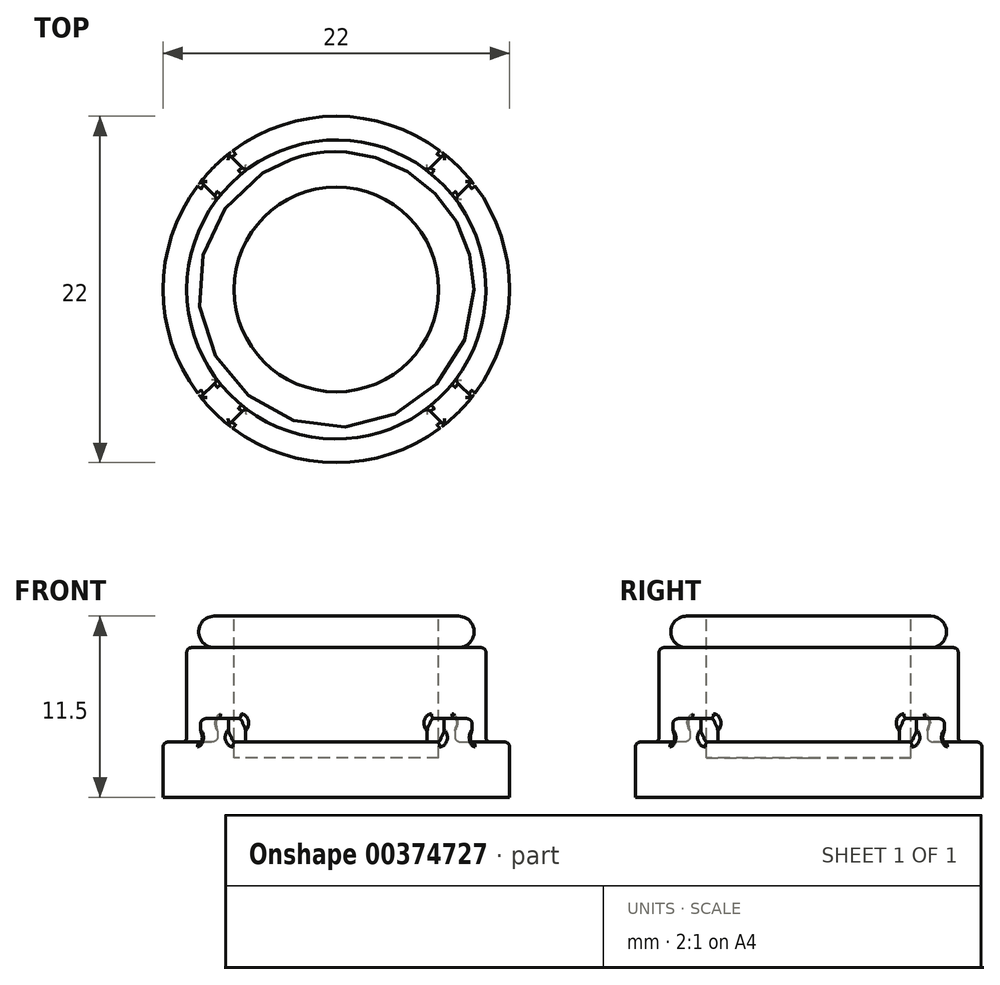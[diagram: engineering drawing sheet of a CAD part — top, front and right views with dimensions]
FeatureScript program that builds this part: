
annotation { "Feature Type Name" : "Feature", "Feature Type Description" : "" }
export const myFeature = defineFeature(function(context is Context, id is Id, definition is map)
    precondition{}
    {
        {
            var Q0;
            Q0=qCreatedBy(makeId("Top.planeOp"),FACE);
            var sketch = newSketch(context, id + "F0", { "sketchPlane" : qUnion([Q0])});
            skCircle(sketch, "E0", {"center": v(0, 0) * mm, "radius": 6.5 * mm});
            skSolve(sketch);
        }
        {
            var Q0;
            Q0 = qSketchRegion(id + "F0", true);
            extrude(context, id + "F1", {"entities" : qUnion([Q0]), "oppositeDirection" : true, "depth" : 9 * mm});
        }
        {
            var Q0;
            Q0=qCreatedBy(makeId("Top.planeOp"),FACE);
            var sketch = newSketch(context, id + "F2", { "sketchPlane" : qUnion([Q0])});
            skCircle(sketch, "E1", {"center": v(0, 0) * mm, "radius": 8.75 * mm});
            skSolve(sketch);
        }
        {
            var Q0;
            Q0 = qSketchRegion(id + "F2", true);
            extrude(context, id + "F3", {"entities" : qUnion([Q0]), "oppositeDirection" : true, "depth" : 2 * mm});
        }
        {
            var Q0;
            Q0=makeQuery(id+"F3.opExtrude","CAP_EDGE",EDGE,{"disambiguationData":[OSD([sQuery(id+"F2.wireOp",EDGE,"E1")])],"isStart":false});
            var Q1;
            Q1=makeQuery(id+"F3.opExtrude","CAP_EDGE",EDGE,{"disambiguationData":[OSD([sQuery(id+"F2.wireOp",EDGE,"E1")])],"isStart":true});
            fillet(context, id + "F4", {"entities" : qUnion([Q0, Q1]), "radius" : 1 * mm, "tangentPropagation" : true, "allowEdgeOverflow" : false});
        }
        {
            var Q0;
            Q0=makeQuery(id+"F3.opExtrude","CAP_FACE",FACE,{"disambiguationData":[OSD([sQuery(id+"F2.wireOp",EDGE,"E1")])],"isStart":false});
            var sketch = newSketch(context, id + "F5", { "sketchPlane" : qUnion([Q0])});
            skCircle(sketch, "E2", {"center": v(0, 0) * mm, "radius": 9.5 * mm});
            skSolve(sketch);
        }
        {
            var Q0;
            Q0 = qSketchRegion(id + "F5", true);
            extrude(context, id + "F6", {"entities" : qUnion([Q0]), "depth" : 6 * mm});
        }
        {
            var Q0;
            Q0=makeQuery(id+"F6.opExtrude","CAP_FACE",FACE,{"disambiguationData":[OSD([sQuery(id+"F5.wireOp",EDGE,"E2")])],"isStart":false});
            var sketch = newSketch(context, id + "F7", { "sketchPlane" : qUnion([Q0])});
            skCircle(sketch, "E3", {"center": v(0, 0) * mm, "radius": 11 * mm});
            skSolve(sketch);
        }
        {
            var Q0;
            Q0 = qSketchRegion(id + "F7", true);
            extrude(context, id + "F8", {"entities" : qUnion([Q0]), "depth" : 3.5 * mm});
        }
        {
            var Q0;
            Q0=makeQuery(id+"F8.opExtrude","CAP_FACE",FACE,{"disambiguationData":[OSD([sQuery(id+"F7.wireOp",EDGE,"E3")])],"isStart":true});
            var sketch = newSketch(context, id + "F9", { "sketchPlane" : qUnion([Q0])});
            skLineSegment(sketch, "E4.bottom", {"start": v(7.78, 7.78) * mm, "end": v(-7.78, 7.78) * mm, "construction": true});
            skLineSegment(sketch, "E4.top", {"start": v(7.78, -7.78) * mm, "end": v(-7.78, -7.78) * mm, "construction": true});
            skLineSegment(sketch, "E4.left", {"start": v(7.78, 7.78) * mm, "end": v(7.78, -7.78) * mm, "construction": true});
            skLineSegment(sketch, "E4.right", {"start": v(-7.78, 7.78) * mm, "end": v(-7.78, -7.78) * mm, "construction": true});
            skPoint(sketch, "E4.middle", {"position": v(0, 0) * mm});
            skLineSegment(sketch, "E5", {"start": v(-7.78, -7.78) * mm, "end": v(7.78, 7.78) * mm, "construction": true});
            skLineSegment(sketch, "E6", {"start": v(-7.78, 7.78) * mm, "end": v(7.78, -7.78) * mm, "construction": true});
            skLineSegment(sketch, "E7.0", {"start": v(-6.84, -8.61) * mm, "end": v(-5.78, -7.54) * mm});
            skLineSegment(sketch, "E8.0", {"start": v(-8.61, -6.84) * mm, "end": v(-7.54, -5.78) * mm});
            skLineSegment(sketch, "E9.0", {"start": v(-8.61, 6.84) * mm, "end": v(-7.54, 5.78) * mm});
            skLineSegment(sketch, "E10.0", {"start": v(-6.84, 8.61) * mm, "end": v(-5.78, 7.54) * mm});
            skArc(sketch, "E11.0", {"start": v(-6.84, 8.61) * mm, "mid": v(-7.78, 7.78) * mm, "end": v(-8.61, 6.84) * mm});
            skArc(sketch, "E12.trimOffspring", {"start": v(-8.61, -6.84) * mm, "mid": v(-7.78, -7.78) * mm, "end": v(-6.84, -8.61) * mm});
            skArc(sketch, "E13.trimOffspring", {"start": v(6.84, -8.61) * mm, "mid": v(7.78, -7.78) * mm, "end": v(8.61, -6.84) * mm});
            skArc(sketch, "E14.trimOffspring", {"start": v(8.61, 6.84) * mm, "mid": v(7.78, 7.78) * mm, "end": v(6.84, 8.61) * mm});
            skArc(sketch, "E15.0", {"start": v(-5.45, 7.78) * mm, "mid": v(-6.72, 6.72) * mm, "end": v(-7.78, 5.45) * mm});
            skArc(sketch, "E16.trimOffspring", {"start": v(7.78, 5.45) * mm, "mid": v(6.72, 6.72) * mm, "end": v(5.45, 7.78) * mm});
            skArc(sketch, "E17.trimOffspring", {"start": v(-7.78, -5.45) * mm, "mid": v(-6.72, -6.72) * mm, "end": v(-5.45, -7.78) * mm});
            skArc(sketch, "E18.trimOffspring", {"start": v(5.45, -7.78) * mm, "mid": v(6.72, -6.72) * mm, "end": v(7.78, -5.45) * mm});
            skLineSegment(sketch, "E19.trimOffspring", {"start": v(0, -1.77) * mm, "end": v(1.77, 0) * mm});
            skLineSegment(sketch, "E20.trimOffspring", {"start": v(-1.77, 0) * mm, "end": v(0, 1.77) * mm});
            skLineSegment(sketch, "E21.trimOffspring", {"start": v(5.78, -7.54) * mm, "end": v(6.84, -8.61) * mm});
            skLineSegment(sketch, "E22.trimOffspring", {"start": v(7.54, -5.78) * mm, "end": v(8.61, -6.84) * mm});
            skLineSegment(sketch, "E23.trimOffspring", {"start": v(7.54, 5.78) * mm, "end": v(8.61, 6.84) * mm});
            skLineSegment(sketch, "E24.trimOffspring", {"start": v(5.78, 7.54) * mm, "end": v(6.84, 8.61) * mm});
            skLineSegment(sketch, "E25.trimOffspring", {"start": v(0, 1.77) * mm, "end": v(1.77, 0) * mm});
            skLineSegment(sketch, "E26.trimOffspring", {"start": v(-1.77, 0) * mm, "end": v(0, -1.77) * mm});
            skSolve(sketch);
        }
        {
            var Q0;
            Q0=makeQuery(id+"F9.imprint","IMPRINT",FACE,{"disambiguationData":[TD([[makeQuery(id+"F9.imprint","IMPRINT",EDGE,{"derivedFrom":sQuery(id+"F9.wireOp",EDGE,"E13.trimOffspring")}),-1.0]])]});
            var Q1;
            Q1=makeQuery(id+"F9.imprint","IMPRINT",FACE,{"disambiguationData":[TD([[makeQuery(id+"F9.imprint","IMPRINT",EDGE,{"derivedFrom":sQuery(id+"F9.wireOp",EDGE,"E14.trimOffspring")}),-1.0]])]});
            var Q2;
            {var subQ0=sQuery(id+"F9.wireOp",EDGE,"E9.0");Q2=makeQuery(id+"F9.imprint","IMPRINT",FACE,{"disambiguationData":[TD([[makeQuery(id+"F9.imprint","IMPRINT",EDGE,{"derivedFrom":subQ0}),1.0]])]});}
            var Q3;
            {var subQ0=sQuery(id+"F9.wireOp",EDGE,"E7.0");Q3=makeQuery(id+"F9.imprint","IMPRINT",FACE,{"disambiguationData":[TD([[makeQuery(id+"F9.imprint","IMPRINT",EDGE,{"derivedFrom":subQ0}),1.0]])]});}
            extrude(context, id + "F10", {"entities" : qUnion([Q0, Q1, Q2, Q3]), "operationType" : NewBodyOperationType.ADD, "depth" : 1.5 * mm});
        }
        {
            var Q0;
            Q0=makeQuery(id+"F6.opExtrude","CAP_EDGE",EDGE,{"disambiguationData":[OSD([sQuery(id+"F5.wireOp",EDGE,"E2")])],"isStart":true});
            var Q1;
            Q1=makeQuery(id+"F10.opExtrude","CAP_FACE",FACE,{"disambiguationData":[OSD([sQuery(id+"F9.wireOp",EDGE,"E7.0"),sQuery(id+"F9.wireOp",EDGE,"E8.0"),sQuery(id+"F9.wireOp",EDGE,"E12.trimOffspring"),sQuery(id+"F9.wireOp",EDGE,"E17.trimOffspring")])],"isStart":false});
            var Q2;
            Q2=makeQuery(id+"F10.opExtrude","CAP_FACE",FACE,{"disambiguationData":[OSD([sQuery(id+"F9.wireOp",EDGE,"E13.trimOffspring"),sQuery(id+"F9.wireOp",EDGE,"E18.trimOffspring"),sQuery(id+"F9.wireOp",EDGE,"E21.trimOffspring"),sQuery(id+"F9.wireOp",EDGE,"E22.trimOffspring")])],"isStart":false});
            var Q3;
            Q3=makeQuery(id+"F8.opExtrude","CAP_FACE",FACE,{"disambiguationData":[OSD([sQuery(id+"F7.wireOp",EDGE,"E3")])],"isStart":true});
            var Q4;
            Q4=makeQuery(id+"F10.opExtrude","CAP_FACE",FACE,{"disambiguationData":[OSD([sQuery(id+"F9.wireOp",EDGE,"E9.0"),sQuery(id+"F9.wireOp",EDGE,"E10.0"),sQuery(id+"F9.wireOp",EDGE,"E11.0"),sQuery(id+"F9.wireOp",EDGE,"E15.0")])],"isStart":false});
            var Q5;
            Q5=makeQuery(id+"F10.opExtrude","CAP_EDGE",EDGE,{"disambiguationData":[OSD([sQuery(id+"F9.wireOp",EDGE,"E16.trimOffspring")])],"isStart":false});
            var Q6;
            Q6=makeQuery(id+"F10.opExtrude","CAP_FACE",FACE,{"disambiguationData":[OSD([sQuery(id+"F9.wireOp",EDGE,"E14.trimOffspring"),sQuery(id+"F9.wireOp",EDGE,"E16.trimOffspring"),sQuery(id+"F9.wireOp",EDGE,"E23.trimOffspring"),sQuery(id+"F9.wireOp",EDGE,"E24.trimOffspring")])],"isStart":false});
            fillet(context, id + "F11", {"entities" : qUnion([Q0, Q1, Q2, Q3, Q4, Q5, Q6]), "radius" : .3 * mm, "tangentPropagation" : true, "allowEdgeOverflow" : false});
        }
    });
